# Revit family: Specialty_Door-Acudor-Flush-PS-5030_Series
name_source: partatom
category: Specialty Equipment
revit_build: Autodesk Revit 2014 (Build: 20130308_1515(x64)
units: mm (PartAtom-declared; Revit-internal decimal feet)

## types (12) — shared parameters
Allen Head Cam Latch = No
Assembly Code = C1020700
Ceiling Mounted = No
Cylinder Lock = No
Default Elevation = 48"
Description = Flush Access Door for Plaster Walls & Ceilings
Finish = Steel-Acudor-14 Gauge-White Alkyd Enamel
Installation Type = Wall Mounted
Length = 2"
Manufacturer = Acudor
Material = Steel-Acudor-White Alkyd Enamel
Mortise Cylinder Lock (Prepare for/or Installed) = No
Product Documentation Link = https://acudor.com
Product Page URL = https://acudor.com
Rim Cylinder Lock = No
Spanner Head Cam Latch = No
Torx Cam Latch = No
URL = http://acudor.com
Wall Mounted = Yes

## per-type parameters (varying)
| type | Array Visibility | First Offset | Height | Latch Count | Latch Spacing | Placeholder | Single Latch Visibility | Width |
| PS-5030 12x12 | No | 2" | 12" | 2 | 4" | 2 | Yes | 12" |
| PS-5030 6x6 | No | 1" | 6" | 2 | 2" | 1 | Yes | 6" |
| PS-5030 8x8 | No | 1 11/32" | 8" | 2 | 2 21/32" | 2 | Yes | 8" |
| PS-5030 10x10 | No | 1 21/32" | 10" | 2 | 3 11/32" | 2 | Yes | 10" |
| PS-5030 14x14 | No | 2 11/32" | 14" | 2 | 4 21/32" | 2 | Yes | 14" |
| PS-5030 16x16 | Yes | 4" | 16" | 2 | 8" | 6 | No | 16" |
| PS-5030 18x18 | Yes | 4 1/2" | 18" | 2 | 9" | 7 | No | 18" |
| PS-5030 22x22 | Yes | 2 3/4" | 22" | 4 | 5 1/2" | 8 | No | 22" |
| PS-5030 24x24 | Yes | 3" | 24" | 4 | 6" | 9 | No | 24" |
| PS-5030 24x36 | Yes | 3 19/32" | 36" | 5 | 7 3/16" | 10 | No | 24" |
| PS-5030 30x30 | Yes | 3" | 30" | 5 | 6" | 11 | No | 30" |
| PS-5030 36x36 | Yes | 3 19/32" | 36" | 5 | 7 3/16" | 12 | No | 36" |

note: column(s) folded — value = type name in every type: Model

## geometry (parser evidence)
native form markers: Sweep x6
no freeform markers — native parametric forms only
